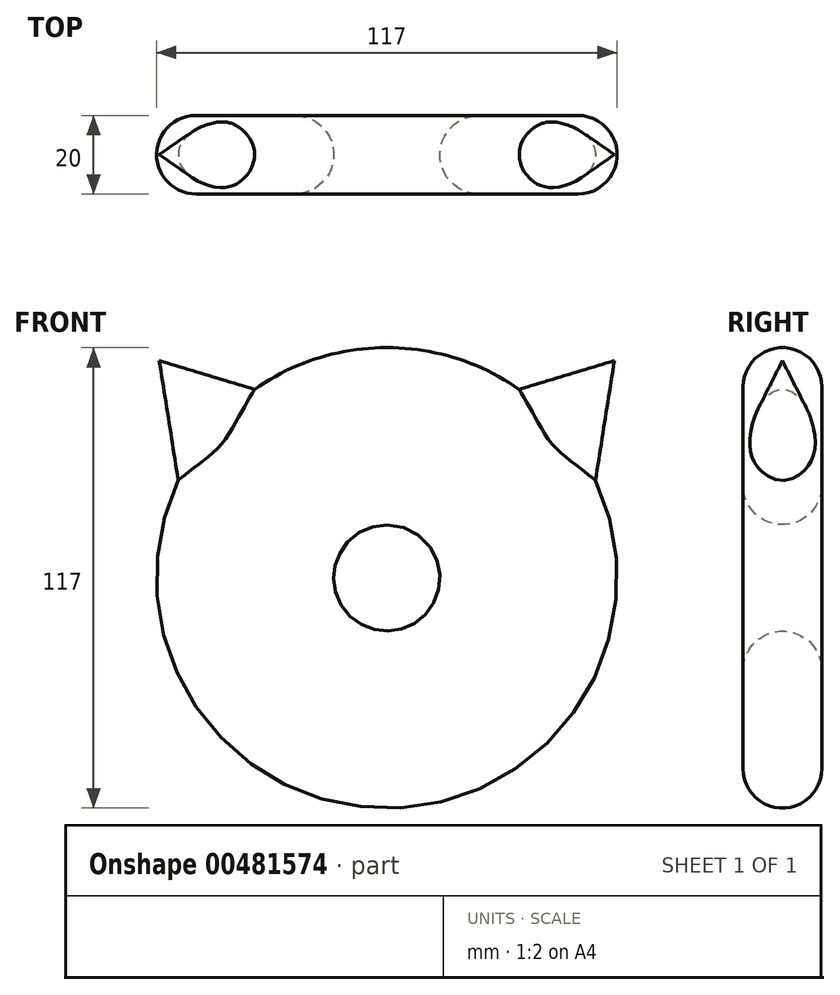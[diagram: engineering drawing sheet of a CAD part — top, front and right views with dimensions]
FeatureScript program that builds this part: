
annotation { "Feature Type Name" : "Feature", "Feature Type Description" : "" }
export const myFeature = defineFeature(function(context is Context, id is Id, definition is map)
    precondition{}
    {
        {
            var Q0;
            Q0=qCreatedBy(makeId("Top.planeOp"),FACE);
            var sketch = newSketch(context, id + "F0", { "sketchPlane" : qUnion([Q0])});
            skCircle(sketch, "E0", {"center": v(-48.5, 0) * mm, "radius": 10 * mm});
            skCircle(sketch, "E1", {"center": v(-23.5, 0) * mm, "radius": 10 * mm});
            skLineSegment(sketch, "E2", {"start": v(-48.5, 10) * mm, "end": v(-23.5, 10) * mm});
            skLineSegment(sketch, "E3", {"start": v(-48.5, -10) * mm, "end": v(-23.5, -10) * mm});
            skSolve(sketch);
        }
        {
            var Q0;
            Q0=qCreatedBy(makeId("Top.planeOp"),FACE);
            var sketch = newSketch(context, id + "F1", { "sketchPlane" : qUnion([Q0])});
            skLineSegment(sketch, "E4", {"start": v(0, 49.98) * mm, "end": v(0, -47.95) * mm});
            skSolve(sketch);
        }
        {
            var Q0;
            Q0 = qSketchRegion(id + "F0", true);
            var Q1;
            Q1=sQuery(id+"F1.wireOp",EDGE,"E4");
            revolve(context, id + "F2", {"entities" : qUnion([Q0]), "axis" : qUnion([Q1]), "revolveType" : RevolveType.FULL});
        }
        {
            var Q0;
            Q0=qCreatedBy(makeId("Front.planeOp"),FACE);
            var sketch = newSketch(context, id + "F3", { "sketchPlane" : qUnion([Q0])});
            skLineSegment(sketch, "E5", {"start": v(-57.83, 55.21) * mm, "end": v(-53.18, 21.5) * mm});
            skLineSegment(sketch, "E6", {"start": v(-53.18, 21.5) * mm, "end": v(-28.77, 46.2) * mm});
            skLineSegment(sketch, "E7", {"start": v(-28.77, 46.2) * mm, "end": v(-57.83, 55.21) * mm});
            skSolve(sketch);
        }
        {
            var Q0;
            Q0=sQuery(id+"F3.wireOp",EDGE,"E6");
            cPlane(context, id + "F4", {"entities" : qUnion([Q0]), "cplaneType" : CPlaneType.LINE_ANGLE, "offset" : 27.1 * mm, "angle" : 90 * degree, "oppositeDirection" : true, "width" : 150 * mm, "height" : 150 * mm});
        }
        {
            var Q0;
            Q0=qCreatedBy(id+"F4.planeOp",FACE);
            var sketch = newSketch(context, id + "F5", { "sketchPlane" : qUnion([Q0])});
            skEllipse(sketch, "E8", {"center": v(0, -4.16) * mm, "majorRadius": 17.05 * mm, "minorRadius": 8.62 * mm, "majorAxis": v(0, 1)});
            skSolve(sketch);
        }
        {
            var Q1;
            Q1=sQuery(id+"F3.wireOp",VERTEX,"E5.start");
            var Q2;
            Q2 = qSketchRegion(id + "F5", true);
            loft(context, id + "F6", {"operationType" : NewBodyOperationType.ADD, "sheetProfilesArray" : [{ "sheetProfileEntities" : qUnion([Q1]) }, { "sheetProfileEntities" : qUnion([Q2]) }]});
        }
        {
            var Q0;
            Q0=makeQuery(id+"F2.opRevolve","SWEPT_BODY",BODY,{"disambiguationData":[OSD([sQuery(id+"F0.wireOp",EDGE,"E0")])]});
            var Q1;
            Q1=qCreatedBy(makeId("Right.planeOp"),FACE);
            mirror(context, id + "F7", {"operationType" : NewBodyOperationType.ADD, "entities" : qUnion([Q0]), "mirrorPlane" : qUnion([Q1])});
        }
    });
